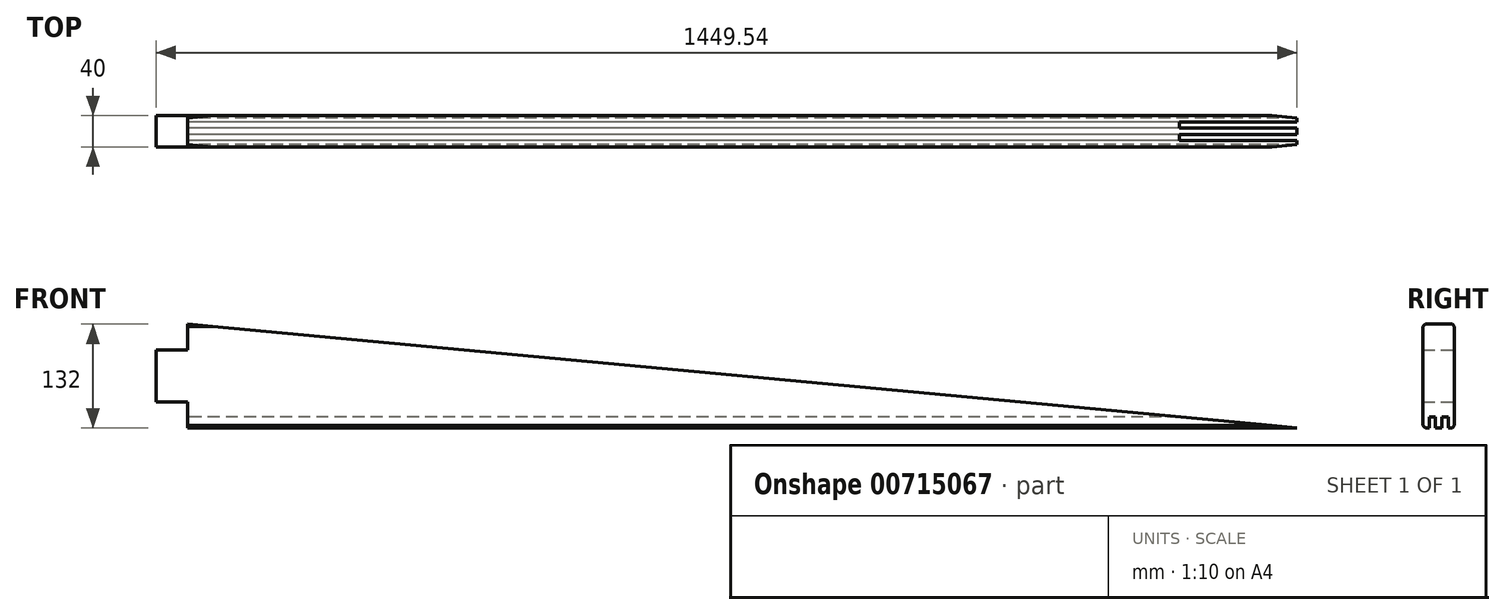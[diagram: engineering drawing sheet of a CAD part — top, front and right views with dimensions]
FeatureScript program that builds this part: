
annotation { "Feature Type Name" : "Feature", "Feature Type Description" : "" }
export const myFeature = defineFeature(function(context is Context, id is Id, definition is map)
    precondition{}
    {
        {
            assignVariable(context, id + "F0", {"name" : "Laenge", "anyValue" : 2550});
        }
        {
            var Q0;
            Q0=qCreatedBy(makeId("Right.planeOp"),FACE);
            var sketch = newSketch(context, id + "F1", { "sketchPlane" : qUnion([Q0])});
            skLineSegment(sketch, "E0", {"start": v(20, 63) * mm, "end": v(20, -63) * mm});
            skLineSegment(sketch, "E1", {"start": v(20, -63) * mm, "end": v(17, -66) * mm});
            skLineSegment(sketch, "E2", {"start": v(17, -66) * mm, "end": v(12, -66) * mm});
            skLineSegment(sketch, "E3", {"start": v(12, -52) * mm, "end": v(12, -66) * mm});
            skLineSegment(sketch, "E4", {"start": v(12, -52) * mm, "end": v(4, -52) * mm});
            skLineSegment(sketch, "E5", {"start": v(4, -66) * mm, "end": v(4, -52) * mm});
            skLineSegment(sketch, "E6", {"start": v(4, -66) * mm, "end": v(-4, -66) * mm});
            skLineSegment(sketch, "E7", {"start": v(-4, -52) * mm, "end": v(-4, -66) * mm});
            skLineSegment(sketch, "E8", {"start": v(-4, -52) * mm, "end": v(-12, -52) * mm});
            skLineSegment(sketch, "E9", {"start": v(-12, -66) * mm, "end": v(-12, -52) * mm});
            skLineSegment(sketch, "E10", {"start": v(-12, -66) * mm, "end": v(-17, -66) * mm});
            skLineSegment(sketch, "E11", {"start": v(-17, -66) * mm, "end": v(-20, -63) * mm});
            skLineSegment(sketch, "E12", {"start": v(-20, -63) * mm, "end": v(-20, 63) * mm});
            skLineSegment(sketch, "E13", {"start": v(-20, 63) * mm, "end": v(-17, 66) * mm});
            skLineSegment(sketch, "E14", {"start": v(-17, 66) * mm, "end": v(-12, 66) * mm});
            skLineSegment(sketch, "E15", {"start": v(-4, 66) * mm, "end": v(4, 66) * mm});
            skLineSegment(sketch, "E16", {"start": v(12, 66) * mm, "end": v(17, 66) * mm});
            skLineSegment(sketch, "E17", {"start": v(17, 66) * mm, "end": v(20, 63) * mm});
            skPoint(sketch, "E18.end.orphan", {"position": v(12, 57.8) * mm});
            skPoint(sketch, "E19.end.orphan", {"position": v(4, 66.3) * mm});
            skPoint(sketch, "E20.end.orphan", {"position": v(-4, 66.3) * mm});
            skLineSegment(sketch, "E21", {"start": v(-12, 66) * mm, "end": v(-12, 80) * mm});
            skLineSegment(sketch, "E22", {"start": v(-12, 80) * mm, "end": v(-4, 80) * mm});
            skLineSegment(sketch, "E23", {"start": v(-4, 80) * mm, "end": v(-4, 66) * mm});
            skLineSegment(sketch, "E24", {"start": v(4, 66) * mm, "end": v(4, 80) * mm});
            skLineSegment(sketch, "E25", {"start": v(4, 80) * mm, "end": v(12, 80) * mm});
            skLineSegment(sketch, "E26", {"start": v(12, 80) * mm, "end": v(12, 66) * mm});
            skLineSegment(sketch, "E27", {"start": v(20, -33) * mm, "end": v(-20, -33) * mm});
            skLineSegment(sketch, "E28", {"start": v(20, 33) * mm, "end": v(-20, 33) * mm});
            skPoint(sketch, "E29.end.orphan", {"position": v(-141.42, 0) * mm});
            skLineSegment(sketch, "E30", {"start": v(20, 0) * mm, "end": v(-20, 0) * mm});
            skLineSegment(sketch, "E31", {"start": v(20, 0) * mm, "end": v(-20, 0) * mm, "construction": true});
            skLineSegment(sketch, "E32", {"start": v(0, 33) * mm, "end": v(0, -33) * mm, "construction": true});
            skSolve(sketch);
        }
        {
            var Q0;
            Q0=qCreatedBy(makeId("Front.planeOp"),FACE);
            var sketch = newSketch(context, id + "F2", { "sketchPlane" : qUnion([Q0])});
            skLineSegment(sketch, "E33", {"start": v(1275, 0) * mm, "end": v(-1275, 0) * mm, "construction": true});
            skPoint(sketch, "E34.right.start.orphan", {"position": v(-259.12, 108.1) * mm});
            skPoint(sketch, "E35.left.start.orphan", {"position": v(237.35, 108.1) * mm});
            skPoint(sketch, "E36.left.end.orphan", {"position": v(237.35, -84.05) * mm});
            skPoint(sketch, "E36.bottom.start.orphan", {"position": v(237.35, -117.05) * mm});
            skPoint(sketch, "E37.right.start.orphan", {"position": v(-259.12, -117.05) * mm});
            skPoint(sketch, "E37.top.end.orphan", {"position": v(-259.12, -84.05) * mm});
            skLineSegment(sketch, "E38.bottom", {"start": v(-1315, 33) * mm, "end": v(-1235, 33) * mm});
            skLineSegment(sketch, "E38.top", {"start": v(-1315, 133) * mm, "end": v(-1235, 133) * mm});
            skLineSegment(sketch, "E38.left", {"start": v(-1315, 33) * mm, "end": v(-1315, 133) * mm});
            skLineSegment(sketch, "E38.right", {"start": v(-1235, 33) * mm, "end": v(-1235, 133) * mm});
            skPoint(sketch, "E38.middle", {"position": v(-1275, 83) * mm});
            skLineSegment(sketch, "E39.bottom", {"start": v(-1315, -133) * mm, "end": v(-1235, -133) * mm});
            skLineSegment(sketch, "E39.top", {"start": v(-1315, -33) * mm, "end": v(-1235, -33) * mm});
            skLineSegment(sketch, "E39.left", {"start": v(-1315, -133) * mm, "end": v(-1315, -33) * mm});
            skLineSegment(sketch, "E39.right", {"start": v(-1235, -133) * mm, "end": v(-1235, -33) * mm});
            skPoint(sketch, "E39.middle", {"position": v(-1275, -83) * mm});
            skLineSegment(sketch, "E40.bottom", {"start": v(1315, 33) * mm, "end": v(1235, 33) * mm});
            skLineSegment(sketch, "E40.top", {"start": v(1315, 133) * mm, "end": v(1235, 133) * mm});
            skLineSegment(sketch, "E40.left", {"start": v(1315, 33) * mm, "end": v(1315, 133) * mm});
            skLineSegment(sketch, "E40.right", {"start": v(1235, 33) * mm, "end": v(1235, 133) * mm});
            skPoint(sketch, "E40.middle", {"position": v(1275, 83) * mm});
            skLineSegment(sketch, "E41.bottom", {"start": v(1315, -33) * mm, "end": v(1235, -33) * mm});
            skLineSegment(sketch, "E41.top", {"start": v(1315, -133) * mm, "end": v(1235, -133) * mm});
            skLineSegment(sketch, "E41.left", {"start": v(1315, -33) * mm, "end": v(1315, -133) * mm});
            skLineSegment(sketch, "E41.right", {"start": v(1235, -33) * mm, "end": v(1235, -133) * mm});
            skPoint(sketch, "E41.middle", {"position": v(1275, -83) * mm});
            skSolve(sketch);
        }
        {
            var Q0;
            {var subQ3=sQuery(id+"F1.wireOp",EDGE,"E13");Q0=makeQuery(id+"F1.imprint","IMPRINT",FACE,{"disambiguationData":[TD([[makeQuery(id+"F1.imprint","IMPRINT",EDGE,{"derivedFrom":subQ3}),-1.0]])]});}
            var Q1;
            {var subQ0=sQuery(id+"F1.wireOp",EDGE,"E28");Q1=makeQuery(id+"F1.imprint","IMPRINT",FACE,{"disambiguationData":[TD([[makeQuery(id+"F1.imprint","IMPRINT",EDGE,{"derivedFrom":subQ0}),1.0]])]});}
            var Q2;
            {var subQ0=sQuery(id+"F1.wireOp",EDGE,"E27");Q2=makeQuery(id+"F1.imprint","IMPRINT",FACE,{"disambiguationData":[TD([[makeQuery(id+"F1.imprint","IMPRINT",EDGE,{"derivedFrom":subQ0}),-1.0]])]});}
            var Q3;
            {var subQ1=sQuery(id+"F1.wireOp",EDGE,"E1");Q3=makeQuery(id+"F1.imprint","IMPRINT",FACE,{"disambiguationData":[TD([[makeQuery(id+"F1.imprint","IMPRINT",EDGE,{"derivedFrom":subQ1}),-1.0]])]});}
            extrude(context, id + "F3", {"entities" : qUnion([Q0, Q1, Q2, Q3]), "endBound" : BoundingType.SYMMETRIC, "depth" : getVariable(context, 'Laenge') * mm, "offsetDistance" : 25 * mm});
        }
        {
            var Q0;
            Q0=makeQuery(id+"F2.imprint","IMPRINT",FACE,{"disambiguationData":[TD([[makeQuery(id+"F2.imprint","IMPRINT",EDGE,{"derivedFrom":sQuery(id+"F2.wireOp",EDGE,"E38.bottom")}),1.0]])]});
            var Q1;
            Q1=makeQuery(id+"F2.imprint","IMPRINT",FACE,{"disambiguationData":[TD([[makeQuery(id+"F2.imprint","IMPRINT",EDGE,{"derivedFrom":sQuery(id+"F2.wireOp",EDGE,"E39.bottom")}),1.0]])]});
            var Q2;
            Q2=makeQuery(id+"F2.imprint","IMPRINT",FACE,{"disambiguationData":[TD([[makeQuery(id+"F2.imprint","IMPRINT",EDGE,{"derivedFrom":sQuery(id+"F2.wireOp",EDGE,"E40.bottom")}),-1.0]])]});
            var Q3;
            Q3=makeQuery(id+"F2.imprint","IMPRINT",FACE,{"disambiguationData":[TD([[makeQuery(id+"F2.imprint","IMPRINT",EDGE,{"derivedFrom":sQuery(id+"F2.wireOp",EDGE,"E41.bottom")}),1.0]])]});
            extrude(context, id + "F4", {"entities" : qUnion([Q0, Q1, Q2, Q3]), "operationType" : NewBodyOperationType.REMOVE, "endBound" : BoundingType.SYMMETRIC, "oppositeDirection" : true, "depth" : 50 * mm, "offsetDistance" : 25 * mm});
        }
        {
            var Q0;
            Q0=makeQuery(id+"F3.opExtrude","SWEPT_FACE",FACE,{"disambiguationData":[OSD([sQuery(id+"F1.wireOp",EDGE,"E12")])]});
            var sketch = newSketch(context, id + "F5", { "sketchPlane" : qUnion([Q0])});
            skLineSegment(sketch, "E42", {"start": v(-1475, 88.48) * mm, "end": v(1525, 88.48) * mm});
            skLineSegment(sketch, "E43", {"start": v(1525, -192.47) * mm, "end": v(-1475, 88.48) * mm});
            skLineSegment(sketch, "E44", {"start": v(1525, 88.48) * mm, "end": v(1525, -192.47) * mm});
            skSolve(sketch);
        }
        {
            var Q0;
            {var subQ6=sQuery(id+"F5.wireOp",EDGE,"E42");Q0=makeQuery(id+"F5.imprint","IMPRINT",FACE,{"disambiguationData":[TD([[makeQuery(id+"F5.imprint","IMPRINT",EDGE,{"derivedFrom":subQ6}),-1.0]])]});}
            var Q1;
            {var subQ0=sQuery(id+"F1.wireOp",EDGE,"E12");Q1=makeQuery(id+"F5.imprint","IMPRINT",FACE,{"disambiguationData":[TD([[makeQuery(id+"F5.imprint","IMPRINT",EDGE,{"derivedFrom":makeQuery(id+"F3.opExtrude","CAP_EDGE",EDGE,{"disambiguationData":[OSD([subQ0])],"isStart":false})}),1.0]])]});}
            extrude(context, id + "F6", {"entities" : qUnion([Q0, Q1]), "operationType" : NewBodyOperationType.REMOVE, "endBound" : BoundingType.SYMMETRIC, "depth" : 100 * mm, "offsetDistance" : 25 * mm});
        }
    });
